# Revit family: PRD_FrankeWS_WshBsnsWsts_DomeWasteValve_ZANMW900
name_source: partatom
category: Plumbing Fixtures
revit_build: Autodesk Revit 2018 (Build: 20190510_1515(x64)
units: mm (PartAtom-declared; Revit-internal decimal feet)

## family parameters
Always vertical = No
Cut with Voids When Loaded = No
Part Type = Normal
Room Calculation Point = No
Round Connector Dimension = Use Diameter
Shared = Yes
Work Plane-Based = Yes

## types (1)
- DomeWasteValve ZANMW900
    AssetType = Fixed
    BIMObjectName = PRD_AR_WashBasinsWastes_RondoWasteValve_DomeWasteValve_ZANMW900
    Category = Pr_70_55_96_97, Wash basins wastes
    Default Elevation = 1219 mm
    Description = Dome waste valve, stainless steel/plastic stem valve, chrome-plated plug, with strainer, connection G 1 1/4 B.
    DurationUnit = year
    Features = Dome waste valve
    GrossWeight = 0.07 kg
    IfcExportAs = IfcWasteTerminalType
    IfcExportType = WASTETRAP
    InletConnectionSize = 0 mm  [stored 0 ft]
    Manufacturer = KWC Group AG
    ManufacturerName = KWC Group AG
    ManufacturerURL = www.kwc.com
    Model = ZANMW900
    ModelNumber = 2000100861
    ModelReference = ZANMW900
    NBSDescription = Wastes for wash basins
    NBSReference = 45-35-70/372
    Name = Dome waste valve ZANMW900
    NetWeight = 0.07 kg
    NominalHeight = 0 mm  [stored 0 ft]
    NominalLength = 0 mm  [stored 0 ft]
    NominalWidth = 0 mm  [stored 0 ft]
    OutletConnectionSize = 32 mm  [stored 0.104987 ft]
    ProductInformation = https://pim.kwc.com
    Shape = Cylindrical
    URL = www.kwc.com
    Uniclass2015Code = Pr_70_55_96_97
    Uniclass2015Title = Wash basins wastes
    Uniclass2015Version = Products v1.7
    Version = 1
    WarrantyDurationUnit = year
    WasteTrapType = Other
    WasteValveMaterial = PRD_AR_StainlessSteel_SatinFinished

note: [stored X ft] marks values corroborated as IEEE doubles in the binary element streams (Revit-internal decimal feet)

## geometry (parser evidence)
native form markers: Sweep x3
no freeform markers — native parametric forms only
